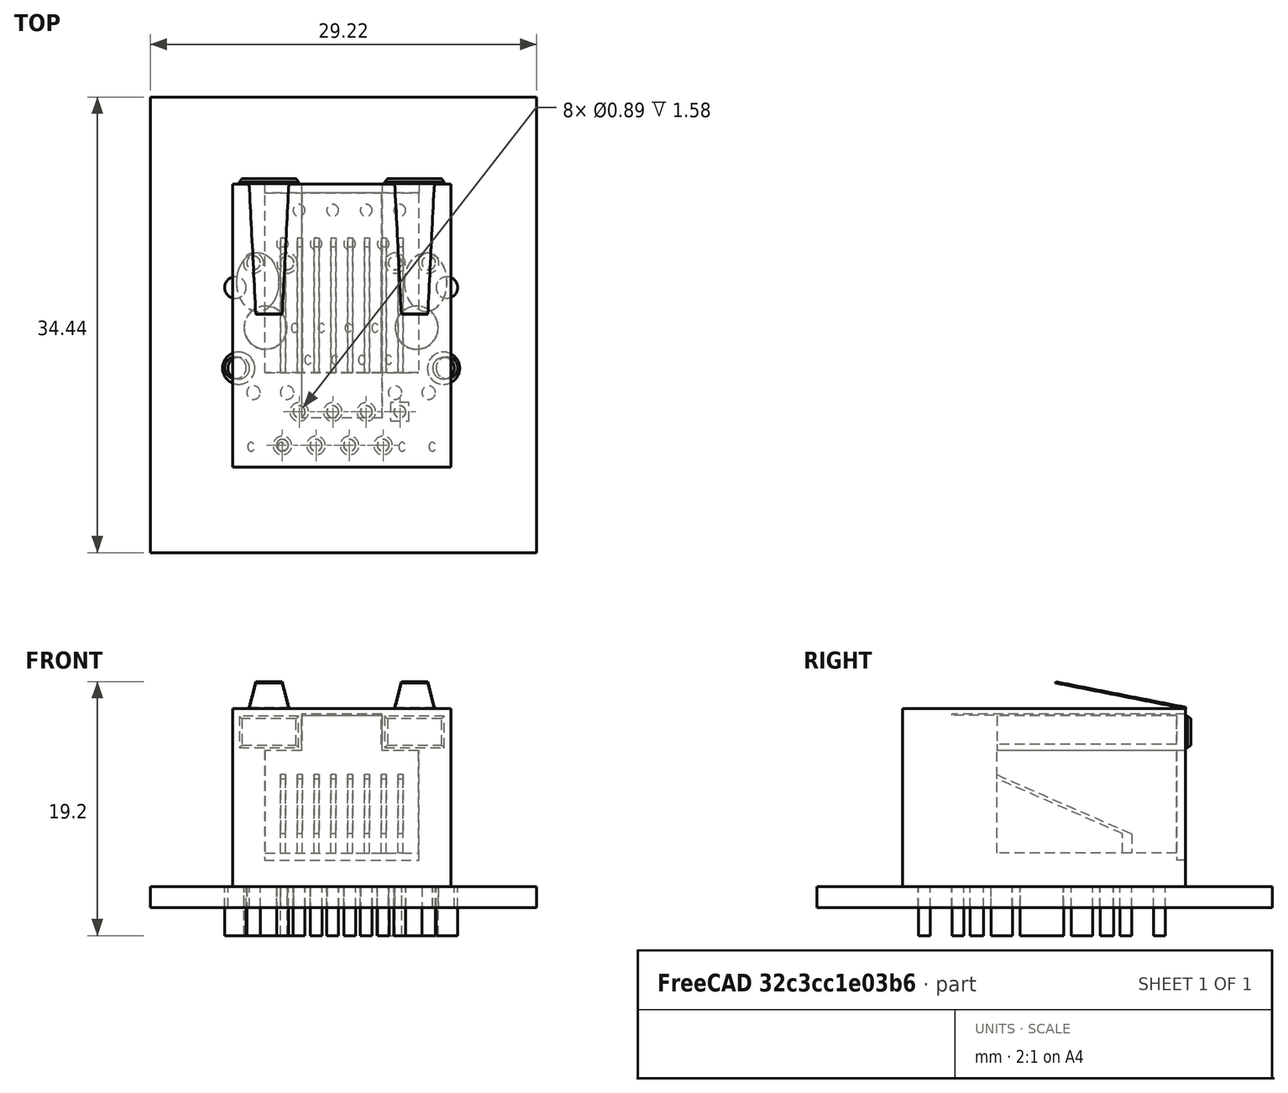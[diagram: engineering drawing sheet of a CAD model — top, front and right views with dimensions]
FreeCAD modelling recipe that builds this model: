
FCSTD DOCUMENT  (FreeCAD 0.19R18353 (Git))
Label: HR9111105A
License: All rights reserved
LicenseURL: http://en.wikipedia.org/wiki/All_rights_reserved
objects: Part::Cylinder×16, Part::FeaturePython×6, Part::Feature×2, App::DocumentObjectGroup×1, Part::Box×1, Part::Cut×1
note: 26 computed .brp shape members not serialized (recipe doc carries the construction recipe); baked Part::Feature solids carry a one-line shape summary decoded from their .brp

FEATURE [Part::FeaturePython] Clone  label="RJ45_Amphenol_RJHSE538X001"  # WARN: FeaturePython — macro-defined, semantics opaque (R4)
  AttacherType = Attacher::AttachEngine3D
  Fuse = false
  Scale = (1,1.36,1)
FEATURE [Part::FeaturePython] Filk_lines  label="FrontSilk"  # a2plus imported part (geometry in sourceFile) (typed FeaturePython)
  fixedPosition = true
FEATURE [Part::FeaturePython] TopPads  # a2plus imported part (geometry in sourceFile) (typed FeaturePython)
  fixedPosition = true
FEATURE [Part::FeaturePython] BotPads  # a2plus imported part (geometry in sourceFile) (typed FeaturePython)
  fixedPosition = true
FEATURE [Part::FeaturePython] THPs  label="PTHs"  # a2plus imported part (geometry in sourceFile) (typed FeaturePython)
  fixedPosition = true
FEATURE [Part::FeaturePython] newPCB  label="Pcb"  # a2plus imported part (geometry in sourceFile) (typed FeaturePython)
  fixedPosition = true
FEATURE [App::DocumentObjectGroup] HANRUN_HR911105A_fp
  Group = -> [Filk_lines,TopPads,BotPads,THPs,newPCB]
FEATURE [Part::Box] Box  label="Cube"
  AttacherType = Attacher::AttachEngine3D
  Height = 10
  Length = 20
  Placement = pos=(-5,-10,-10) rot=(0,0,1;0rad)
  Width = 20
FEATURE [Part::Cut] Cut
  Base = -> Clone
  Placement = pos=(-3.5,0,0) rot=(0,0,1;0rad)
  Tool = -> Box
FEATURE [Part::Cylinder] cylinder
  Angle = 360
  AttacherType = Attacher::AttachEngine3D
  Height = 3.7
  Placement = pos=(5.715,0,-3.7) rot=(0,0,1;0rad)
  Radius = 1.625
FEATURE [Part::Cylinder] cylinder001
  Angle = 360
  AttacherType = Attacher::AttachEngine3D
  Height = 3.7
  Placement = pos=(-5.715,0,-3.7) rot=(0,0,1;0rad)
  Radius = 1.625
FEATURE [Part::Cylinder] cylinder002
  Angle = 360
  AttacherType = Attacher::AttachEngine3D
  Height = 3.7
  Placement = pos=(6.625,-4.9,-3.7) rot=(0,0,1;0rad)
  Radius = 0.51
FEATURE [Part::Cylinder] cylinder003
  Angle = 360
  AttacherType = Attacher::AttachEngine3D
  Height = 3.7
  Placement = pos=(-6.625,-4.9,-3.7) rot=(0,0,1;0rad)
  Radius = 0.51
FEATURE [Part::Cylinder] cylinder004
  Angle = 360
  AttacherType = Attacher::AttachEngine3D
  Height = 3.7
  Placement = pos=(4.085,-4.9,-3.7) rot=(0,0,1;0rad)
  Radius = 0.51
FEATURE [Part::Cylinder] cylinder005
  Angle = 360
  AttacherType = Attacher::AttachEngine3D
  Height = 3.7
  Placement = pos=(-4.085,-4.9,-3.7) rot=(0,0,1;0rad)
  Radius = 0.51
FEATURE [Part::Cylinder] cylinder006
  Angle = 360
  AttacherType = Attacher::AttachEngine3D
  Height = 3.7
  Placement = pos=(8,3.05,-3.7) rot=(0,0,1;0rad)
  Radius = 0.815
FEATURE [Part::Cylinder] cylinder007
  Angle = 360
  AttacherType = Attacher::AttachEngine3D
  Height = 3.7
  Placement = pos=(-8,3.05,-3.7) rot=(0,0,1;0rad)
  Radius = 0.815
FEATURE [Part::Cylinder] cylinder008
  Angle = 360
  AttacherType = Attacher::AttachEngine3D
  Height = 3.7
  Placement = pos=(0.64,6.35,-3.7) rot=(0,0,1;0rad)
  Radius = 0.445
FEATURE [Part::Cylinder] cylinder009
  Angle = 360
  AttacherType = Attacher::AttachEngine3D
  Height = 3.7
  Placement = pos=(3.18,6.35,-3.7) rot=(0,0,1;0rad)
  Radius = 0.445
FEATURE [Part::Cylinder] cylinder010
  Angle = 360
  AttacherType = Attacher::AttachEngine3D
  Height = 3.7
  Placement = pos=(-1.9,6.35,-3.7) rot=(0,0,1;0rad)
  Radius = 0.445
FEATURE [Part::Cylinder] cylinder011
  Angle = 360
  AttacherType = Attacher::AttachEngine3D
  Height = 3.7
  Placement = pos=(-4.44,6.35,-3.7) rot=(0,0,1;0rad)
  Radius = 0.445
FEATURE [Part::Cylinder] cylinder012
  Angle = 360
  AttacherType = Attacher::AttachEngine3D
  Height = 3.7
  Placement = pos=(-0.64,8.89,-3.7) rot=(0,0,1;0rad)
  Radius = 0.445
FEATURE [Part::Cylinder] cylinder013
  Angle = 360
  AttacherType = Attacher::AttachEngine3D
  Height = 3.7
  Placement = pos=(-3.18,8.89,-3.7) rot=(0,0,1;0rad)
  Radius = 0.445
FEATURE [Part::Cylinder] cylinder014
  Angle = 360
  AttacherType = Attacher::AttachEngine3D
  Height = 3.7
  Placement = pos=(1.9,8.89,-3.7) rot=(0,0,1;0rad)
  Radius = 0.445
FEATURE [Part::Cylinder] cylinder015
  Angle = 360
  AttacherType = Attacher::AttachEngine3D
  Height = 3.7
  Placement = pos=(4.44,8.89,-3.7) rot=(0,0,1;0rad)
  Radius = 0.445
FEATURE [Part::Feature] Shape001  label="Fusion"
  shape: bbox 17.63 x 14.75 x 3.7 mm, 48 faces, 16 solids (baked)
FEATURE [Part::Feature] Shape  label="Fusion001"
  shape: bbox 17.63 x 21.83 x 19.2 mm, 165 faces, 3 solids (baked)
